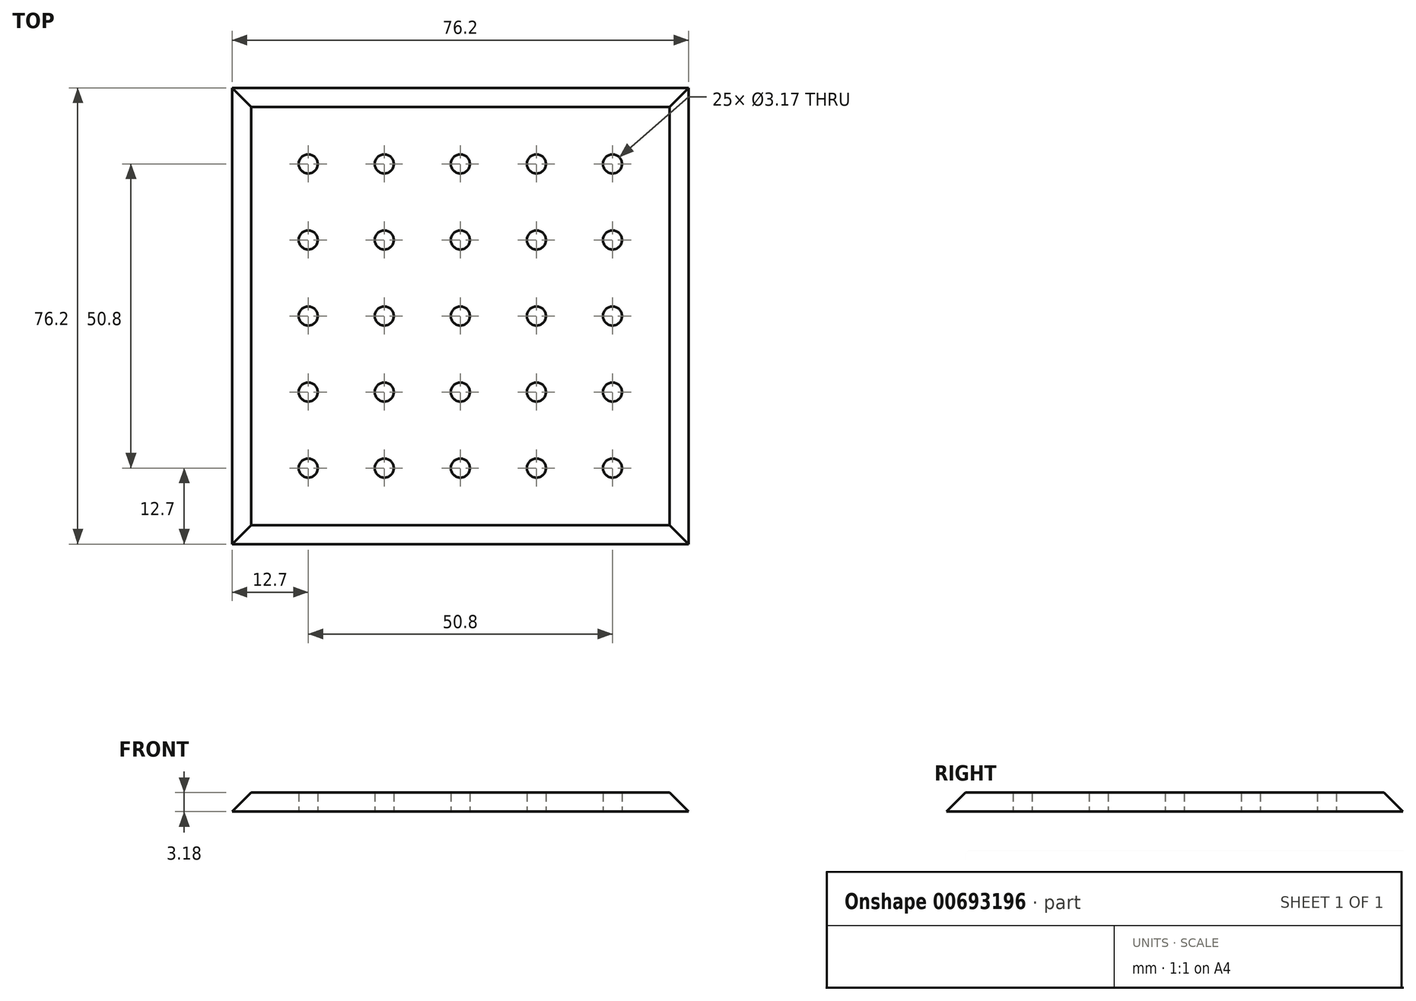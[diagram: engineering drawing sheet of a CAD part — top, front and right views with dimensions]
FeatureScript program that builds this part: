
annotation { "Feature Type Name" : "Feature", "Feature Type Description" : "" }
export const myFeature = defineFeature(function(context is Context, id is Id, definition is map)
    precondition{}
    {
        {
            var Q0;
            Q0=qCreatedBy(makeId("Top.planeOp"),FACE);
            var sketch = newSketch(context, id + "F0", { "sketchPlane" : qUnion([Q0])});
            skLineSegment(sketch, "E0.bottom", {"start": v(38.1, 38.1) * mm, "end": v(-38.1, 38.1) * mm});
            skLineSegment(sketch, "E0.top", {"start": v(38.1, -38.1) * mm, "end": v(-38.1, -38.1) * mm});
            skLineSegment(sketch, "E0.left", {"start": v(38.1, 38.1) * mm, "end": v(38.1, -38.1) * mm});
            skLineSegment(sketch, "E0.right", {"start": v(-38.1, 38.1) * mm, "end": v(-38.1, -38.1) * mm});
            skPoint(sketch, "E0.middle", {"position": v(0, 0) * mm});
            skSolve(sketch);
        }
        {
            var Q0;
            Q0=qSketchRegion(id+"F0",true);
            extrude(context, id + "F1", {"entities" : qUnion([Q0]), "depth" : 3.17 * mm, "offsetDistance" : 25.4 * mm});
        }
        {
            var Q0;
            Q0=makeQuery(id+"F1.opExtrude","SWEPT_FACE",FACE,{"disambiguationData":[OSD([sQuery(id+"F0.wireOp",EDGE,"E0.left")])]});
            var sketch = newSketch(context, id + "F2", { "sketchPlane" : qUnion([Q0])});
            skLineSegment(sketch, "E1", {"start": v(-38.1, 0) * mm, "end": v(-34.93, 3.17) * mm});
            skLineSegment(sketch, "E2", {"start": v(-34.93, 3.17) * mm, "end": v(-38.1, 3.18) * mm});
            skLineSegment(sketch, "E3", {"start": v(-38.1, 3.18) * mm, "end": v(-38.1, 0) * mm});
            skLineSegment(sketch, "E4", {"start": v(0, 12.24) * mm, "end": v(0, -11.06) * mm, "construction": true});
            skLineSegment(sketch, "E5.MirrorCS", {"start": v(38.1, 0) * mm, "end": v(34.93, 3.17) * mm});
            skLineSegment(sketch, "E6.MirrorCS", {"start": v(34.93, 3.17) * mm, "end": v(38.1, 3.18) * mm});
            skLineSegment(sketch, "E7.MirrorCS", {"start": v(38.1, 3.18) * mm, "end": v(38.1, 0) * mm});
            skSolve(sketch);
        }
        {
            var Q0;
            Q0=makeQuery(id+"F1.opExtrude","SWEPT_FACE",FACE,{"disambiguationData":[OSD([sQuery(id+"F0.wireOp",EDGE,"E0.bottom")])]});
            var sketch = newSketch(context, id + "F3", { "sketchPlane" : qUnion([Q0])});
            skLineSegment(sketch, "E8", {"start": v(-38.1, 0) * mm, "end": v(-34.93, 3.17) * mm});
            skLineSegment(sketch, "E9", {"start": v(-34.93, 3.18) * mm, "end": v(-38.1, 3.18) * mm});
            skLineSegment(sketch, "E10", {"start": v(-38.1, 3.18) * mm, "end": v(-38.1, 0) * mm});
            skLineSegment(sketch, "E11", {"start": v(0, 8.91) * mm, "end": v(0, -4.58) * mm, "construction": true});
            skLineSegment(sketch, "E12.MirrorCS", {"start": v(38.1, 0) * mm, "end": v(34.93, 3.17) * mm});
            skLineSegment(sketch, "E13.MirrorCS", {"start": v(34.93, 3.18) * mm, "end": v(38.1, 3.18) * mm});
            skLineSegment(sketch, "E14.MirrorCS", {"start": v(38.1, 3.18) * mm, "end": v(38.1, 0) * mm});
            skSolve(sketch);
        }
        {
            var Q0;
            Q0=makeQuery(id+"F3.imprint","IMPRINT",FACE,{"disambiguationData":[TD([[makeQuery(id+"F3.imprint","IMPRINT",EDGE,{"derivedFrom":sQuery(id+"F3.wireOp",EDGE,"E8")}),1.0]])]});
            var Q1;
            Q1=makeQuery(id+"F3.imprint","IMPRINT",FACE,{"disambiguationData":[TD([[makeQuery(id+"F3.imprint","IMPRINT",EDGE,{"derivedFrom":sQuery(id+"F3.wireOp",EDGE,"E12.MirrorCS")}),-1.0]])]});
            extrude(context, id + "F4", {"entities" : qUnion([Q0, Q1]), "operationType" : NewBodyOperationType.REMOVE, "oppositeDirection" : true, "depth" : 76.2 * mm, "offsetDistance" : 25.4 * mm});
        }
        {
            var Q0;
            Q0=makeQuery(id+"F2.imprint","IMPRINT",FACE,{"disambiguationData":[TD([[makeQuery(id+"F2.imprint","IMPRINT",EDGE,{"derivedFrom":sQuery(id+"F2.wireOp",EDGE,"E5.MirrorCS")}),-1.0]])]});
            var Q1;
            Q1=makeQuery(id+"F2.imprint","IMPRINT",FACE,{"disambiguationData":[TD([[makeQuery(id+"F2.imprint","IMPRINT",EDGE,{"derivedFrom":sQuery(id+"F2.wireOp",EDGE,"E1")}),1.0]])]});
            extrude(context, id + "F5", {"entities" : qUnion([Q0, Q1]), "operationType" : NewBodyOperationType.REMOVE, "oppositeDirection" : true, "depth" : 76.2 * mm, "offsetDistance" : 25.4 * mm});
        }
        {
            var Q0;
            Q0=makeQuery(id+"F1.opExtrude","CAP_FACE",FACE,{"disambiguationData":[OSD([sQuery(id+"F0.wireOp",EDGE,"E0.bottom"),sQuery(id+"F0.wireOp",EDGE,"E0.top"),sQuery(id+"F0.wireOp",EDGE,"E0.left"),sQuery(id+"F0.wireOp",EDGE,"E0.right")])],"isStart":true});
            var sketch = newSketch(context, id + "F6", { "sketchPlane" : qUnion([Q0])});
            skCircle(sketch, "E15", {"center": v(-25.4, 25.4) * mm, "radius": 1.59 * mm});
            skCircle(sketch, "E16.0.1.0", {"center": v(-25.4, 12.7) * mm, "radius": 1.59 * mm});
            skCircle(sketch, "E16.0.2.0", {"center": v(-25.4, 0) * mm, "radius": 1.59 * mm});
            skCircle(sketch, "E16.0.3.0", {"center": v(-25.4, -12.7) * mm, "radius": 1.59 * mm});
            skCircle(sketch, "E16.0.4.0", {"center": v(-25.4, -25.4) * mm, "radius": 1.59 * mm});
            skCircle(sketch, "E16.1.0.0", {"center": v(-12.7, 25.4) * mm, "radius": 1.59 * mm});
            skCircle(sketch, "E16.1.1.0", {"center": v(-12.7, 12.7) * mm, "radius": 1.59 * mm});
            skCircle(sketch, "E16.1.2.0", {"center": v(-12.7, 0) * mm, "radius": 1.59 * mm});
            skCircle(sketch, "E16.1.3.0", {"center": v(-12.7, -12.7) * mm, "radius": 1.59 * mm});
            skCircle(sketch, "E16.1.4.0", {"center": v(-12.7, -25.4) * mm, "radius": 1.59 * mm});
            skCircle(sketch, "E16.2.0.0", {"center": v(0, 25.4) * mm, "radius": 1.59 * mm});
            skCircle(sketch, "E16.2.1.0", {"center": v(0, 12.7) * mm, "radius": 1.59 * mm});
            skCircle(sketch, "E16.2.2.0", {"center": v(0, 0) * mm, "radius": 1.59 * mm});
            skCircle(sketch, "E16.2.3.0", {"center": v(0, -12.7) * mm, "radius": 1.59 * mm});
            skCircle(sketch, "E16.2.4.0", {"center": v(0, -25.4) * mm, "radius": 1.59 * mm});
            skCircle(sketch, "E16.3.0.0", {"center": v(12.7, 25.4) * mm, "radius": 1.59 * mm});
            skCircle(sketch, "E16.3.1.0", {"center": v(12.7, 12.7) * mm, "radius": 1.59 * mm});
            skCircle(sketch, "E16.3.2.0", {"center": v(12.7, 0) * mm, "radius": 1.59 * mm});
            skCircle(sketch, "E16.3.3.0", {"center": v(12.7, -12.7) * mm, "radius": 1.59 * mm});
            skCircle(sketch, "E16.3.4.0", {"center": v(12.7, -25.4) * mm, "radius": 1.59 * mm});
            skCircle(sketch, "E16.4.0.0", {"center": v(25.4, 25.4) * mm, "radius": 1.59 * mm});
            skCircle(sketch, "E16.4.1.0", {"center": v(25.4, 12.7) * mm, "radius": 1.59 * mm});
            skCircle(sketch, "E16.4.2.0", {"center": v(25.4, 0) * mm, "radius": 1.59 * mm});
            skCircle(sketch, "E16.4.3.0", {"center": v(25.4, -12.7) * mm, "radius": 1.59 * mm});
            skCircle(sketch, "E16.4.4.0", {"center": v(25.4, -25.4) * mm, "radius": 1.59 * mm});
            skLineSegment(sketch, "E16.direction1", {"start": v(-25.4, 25.4) * mm, "end": v(-12.7, 25.4) * mm, "construction": true});
            skLineSegment(sketch, "E16.direction2", {"start": v(-25.4, 25.4) * mm, "end": v(-25.4, 12.7) * mm, "construction": true});
            skSolve(sketch);
        }
        {
            var Q0;
            Q0=makeQuery(id+"F6.imprint","IMPRINT",FACE,{"disambiguationData":[TD([[makeQuery(id+"F6.imprint","IMPRINT",EDGE,{"derivedFrom":sQuery(id+"F6.wireOp",EDGE,"E15")}),1.0]])]});
            var Q1;
            Q1=makeQuery(id+"F6.imprint","IMPRINT",FACE,{"disambiguationData":[TD([[makeQuery(id+"F6.imprint","IMPRINT",EDGE,{"derivedFrom":sQuery(id+"F6.wireOp",EDGE,"E16.1.0.0")}),1.0]])]});
            var Q2;
            Q2=makeQuery(id+"F6.imprint","IMPRINT",FACE,{"disambiguationData":[TD([[makeQuery(id+"F6.imprint","IMPRINT",EDGE,{"derivedFrom":sQuery(id+"F6.wireOp",EDGE,"E16.3.0.0")}),1.0]])]});
            var Q3;
            Q3=makeQuery(id+"F6.imprint","IMPRINT",FACE,{"disambiguationData":[TD([[makeQuery(id+"F6.imprint","IMPRINT",EDGE,{"derivedFrom":sQuery(id+"F6.wireOp",EDGE,"E16.4.0.0")}),1.0]])]});
            var Q4;
            Q4=makeQuery(id+"F6.imprint","IMPRINT",FACE,{"disambiguationData":[TD([[makeQuery(id+"F6.imprint","IMPRINT",EDGE,{"derivedFrom":sQuery(id+"F6.wireOp",EDGE,"E16.2.0.0")}),1.0]])]});
            var Q5;
            Q5=makeQuery(id+"F6.imprint","IMPRINT",FACE,{"disambiguationData":[TD([[makeQuery(id+"F6.imprint","IMPRINT",EDGE,{"derivedFrom":sQuery(id+"F6.wireOp",EDGE,"E16.2.1.0")}),1.0]])]});
            var Q6;
            Q6=makeQuery(id+"F6.imprint","IMPRINT",FACE,{"disambiguationData":[TD([[makeQuery(id+"F6.imprint","IMPRINT",EDGE,{"derivedFrom":sQuery(id+"F6.wireOp",EDGE,"E16.1.1.0")}),1.0]])]});
            var Q7;
            Q7=makeQuery(id+"F6.imprint","IMPRINT",FACE,{"disambiguationData":[TD([[makeQuery(id+"F6.imprint","IMPRINT",EDGE,{"derivedFrom":sQuery(id+"F6.wireOp",EDGE,"E16.0.1.0")}),1.0]])]});
            var Q8;
            Q8=makeQuery(id+"F6.imprint","IMPRINT",FACE,{"disambiguationData":[TD([[makeQuery(id+"F6.imprint","IMPRINT",EDGE,{"derivedFrom":sQuery(id+"F6.wireOp",EDGE,"E16.0.2.0")}),1.0]])]});
            var Q9;
            Q9=makeQuery(id+"F6.imprint","IMPRINT",FACE,{"disambiguationData":[TD([[makeQuery(id+"F6.imprint","IMPRINT",EDGE,{"derivedFrom":sQuery(id+"F6.wireOp",EDGE,"E16.1.2.0")}),1.0]])]});
            var Q10;
            Q10=makeQuery(id+"F6.imprint","IMPRINT",FACE,{"disambiguationData":[TD([[makeQuery(id+"F6.imprint","IMPRINT",EDGE,{"derivedFrom":sQuery(id+"F6.wireOp",EDGE,"E16.2.2.0")}),1.0]])]});
            var Q11;
            Q11=makeQuery(id+"F6.imprint","IMPRINT",FACE,{"disambiguationData":[TD([[makeQuery(id+"F6.imprint","IMPRINT",EDGE,{"derivedFrom":sQuery(id+"F6.wireOp",EDGE,"E16.3.1.0")}),1.0]])]});
            var Q12;
            Q12=makeQuery(id+"F6.imprint","IMPRINT",FACE,{"disambiguationData":[TD([[makeQuery(id+"F6.imprint","IMPRINT",EDGE,{"derivedFrom":sQuery(id+"F6.wireOp",EDGE,"E16.4.1.0")}),1.0]])]});
            var Q13;
            Q13=makeQuery(id+"F6.imprint","IMPRINT",FACE,{"disambiguationData":[TD([[makeQuery(id+"F6.imprint","IMPRINT",EDGE,{"derivedFrom":sQuery(id+"F6.wireOp",EDGE,"E16.4.2.0")}),1.0]])]});
            var Q14;
            Q14=makeQuery(id+"F6.imprint","IMPRINT",FACE,{"disambiguationData":[TD([[makeQuery(id+"F6.imprint","IMPRINT",EDGE,{"derivedFrom":sQuery(id+"F6.wireOp",EDGE,"E16.3.2.0")}),1.0]])]});
            var Q15;
            Q15=makeQuery(id+"F6.imprint","IMPRINT",FACE,{"disambiguationData":[TD([[makeQuery(id+"F6.imprint","IMPRINT",EDGE,{"derivedFrom":sQuery(id+"F6.wireOp",EDGE,"E16.0.3.0")}),1.0]])]});
            var Q16;
            Q16=makeQuery(id+"F6.imprint","IMPRINT",FACE,{"disambiguationData":[TD([[makeQuery(id+"F6.imprint","IMPRINT",EDGE,{"derivedFrom":sQuery(id+"F6.wireOp",EDGE,"E16.0.4.0")}),1.0]])]});
            var Q17;
            Q17=makeQuery(id+"F6.imprint","IMPRINT",FACE,{"disambiguationData":[TD([[makeQuery(id+"F6.imprint","IMPRINT",EDGE,{"derivedFrom":sQuery(id+"F6.wireOp",EDGE,"E16.1.4.0")}),1.0]])]});
            var Q18;
            Q18=makeQuery(id+"F6.imprint","IMPRINT",FACE,{"disambiguationData":[TD([[makeQuery(id+"F6.imprint","IMPRINT",EDGE,{"derivedFrom":sQuery(id+"F6.wireOp",EDGE,"E16.2.4.0")}),1.0]])]});
            var Q19;
            Q19=makeQuery(id+"F6.imprint","IMPRINT",FACE,{"disambiguationData":[TD([[makeQuery(id+"F6.imprint","IMPRINT",EDGE,{"derivedFrom":sQuery(id+"F6.wireOp",EDGE,"E16.3.4.0")}),1.0]])]});
            var Q20;
            Q20=makeQuery(id+"F6.imprint","IMPRINT",FACE,{"disambiguationData":[TD([[makeQuery(id+"F6.imprint","IMPRINT",EDGE,{"derivedFrom":sQuery(id+"F6.wireOp",EDGE,"E16.4.4.0")}),1.0]])]});
            var Q21;
            Q21=makeQuery(id+"F6.imprint","IMPRINT",FACE,{"disambiguationData":[TD([[makeQuery(id+"F6.imprint","IMPRINT",EDGE,{"derivedFrom":sQuery(id+"F6.wireOp",EDGE,"E16.4.3.0")}),1.0]])]});
            var Q22;
            Q22=makeQuery(id+"F6.imprint","IMPRINT",FACE,{"disambiguationData":[TD([[makeQuery(id+"F6.imprint","IMPRINT",EDGE,{"derivedFrom":sQuery(id+"F6.wireOp",EDGE,"E16.3.3.0")}),1.0]])]});
            var Q23;
            Q23=makeQuery(id+"F6.imprint","IMPRINT",FACE,{"disambiguationData":[TD([[makeQuery(id+"F6.imprint","IMPRINT",EDGE,{"derivedFrom":sQuery(id+"F6.wireOp",EDGE,"E16.2.3.0")}),1.0]])]});
            var Q24;
            Q24=makeQuery(id+"F6.imprint","IMPRINT",FACE,{"disambiguationData":[TD([[makeQuery(id+"F6.imprint","IMPRINT",EDGE,{"derivedFrom":sQuery(id+"F6.wireOp",EDGE,"E16.1.3.0")}),1.0]])]});
            extrude(context, id + "F7", {"entities" : qUnion([Q0, Q1, Q2, Q3, Q4, Q5, Q6, Q7, Q8, Q9, Q10, Q11, Q12, Q13, Q14, Q15, Q16, Q17, Q18, Q19, Q20, Q21, Q22, Q23, Q24]), "operationType" : NewBodyOperationType.REMOVE, "endBound" : BoundingType.THROUGH_ALL, "oppositeDirection" : true, "depth" : 25.4 * mm, "offsetDistance" : 25.4 * mm});
        }
    });
